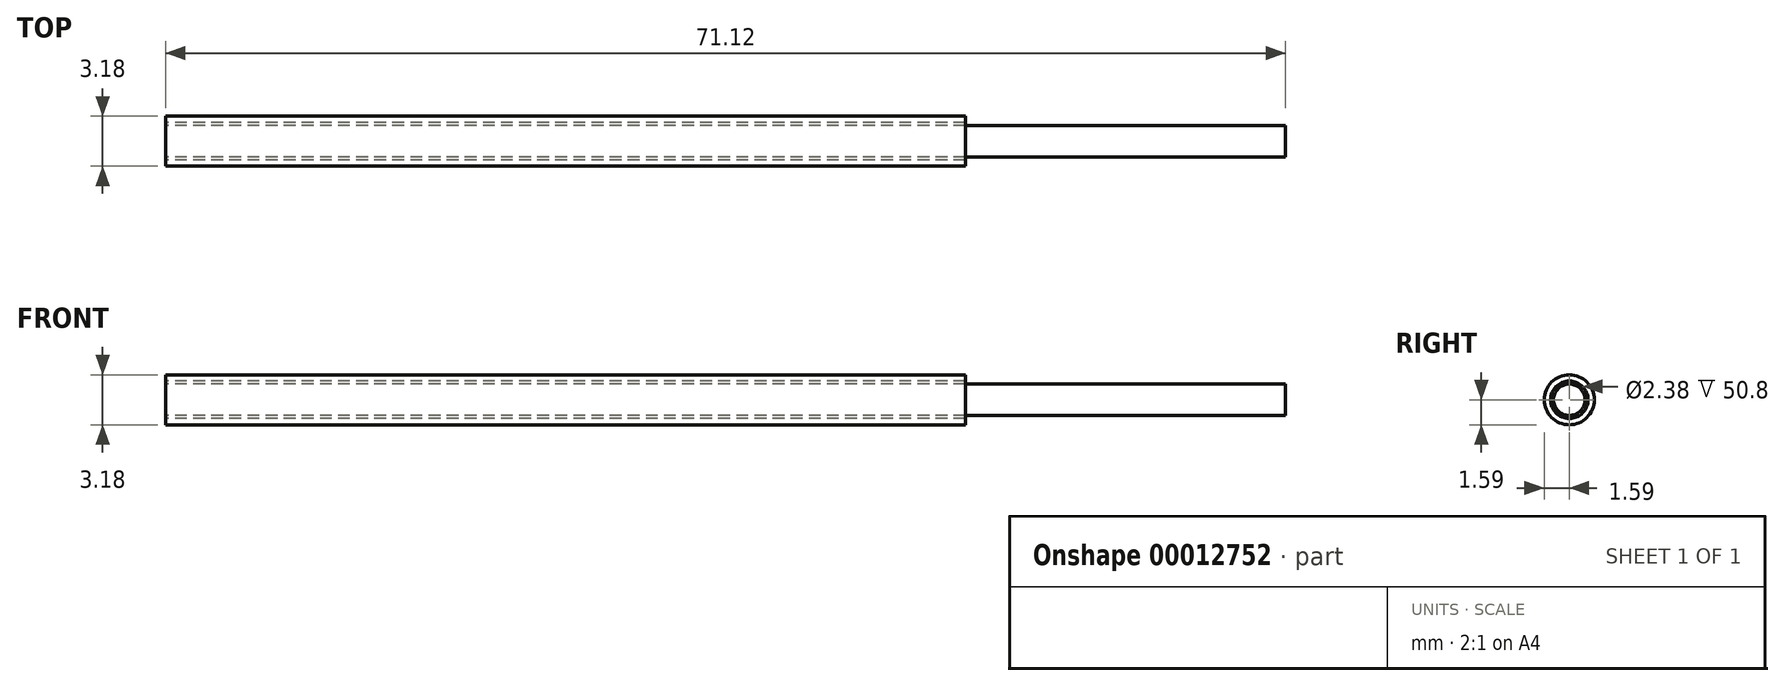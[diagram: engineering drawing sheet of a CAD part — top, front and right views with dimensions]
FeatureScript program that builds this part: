
annotation { "Feature Type Name" : "Feature", "Feature Type Description" : "" }
export const myFeature = defineFeature(function(context is Context, id is Id, definition is map)
    precondition{}
    {
        {
            var Q0;
            Q0=qCreatedBy(makeId("Right.planeOp"),FACE);
            var sketch = newSketch(context, id + "F0", { "sketchPlane" : qUnion([Q0])});
            skCircle(sketch, "E0", {"center": v(0, 0) * mm, "radius": 1.59 * mm});
            skCircle(sketch, "E1", {"center": v(0, 0) * mm, "radius": 1.2 * mm});
            skSolve(sketch);
        }
        {
            var Q0;
            Q0=makeQuery(id+"F0.imprint","IMPRINT",FACE,{"disambiguationData":[TD([[makeQuery(id+"F0.imprint","IMPRINT",EDGE,{"derivedFrom":sQuery(id+"F0.wireOp",EDGE,"E0")}),1.0]])]});
            extrude(context, id + "F1", {"entities" : qUnion([Q0]), "depth" : 50.8 * mm});
        }
        {
            var Q0;
            Q0=qCreatedBy(makeId("Right.planeOp"),FACE);
            var sketch = newSketch(context, id + "F2", { "sketchPlane" : qUnion([Q0])});
            skCircle(sketch, "E2", {"center": v(0, 0) * mm, "radius": 1 * mm});
            skSolve(sketch);
        }
        {
            var Q0;
            Q0=makeQuery(id+"F2.imprint","IMPRINT",FACE,{"disambiguationData":[TD([[makeQuery(id+"F2.imprint","IMPRINT",EDGE,{"derivedFrom":sQuery(id+"F2.wireOp",EDGE,"E2")}),1.0]])]});
            extrude(context, id + "F3", {"entities" : qUnion([Q0]), "depth" : 71.12 * mm});
        }
    });
